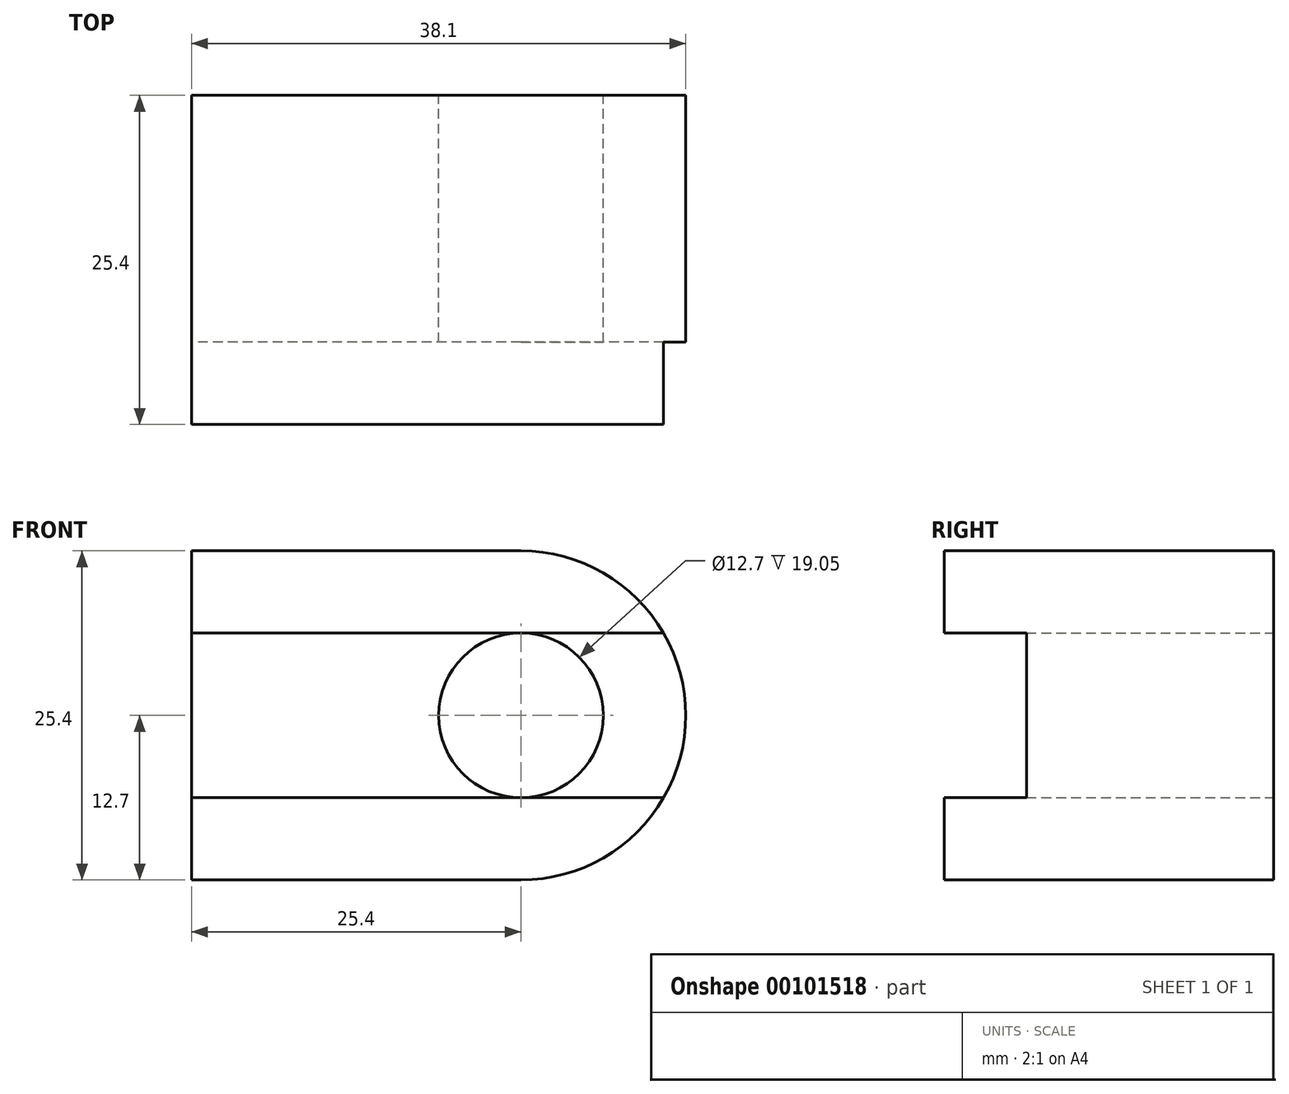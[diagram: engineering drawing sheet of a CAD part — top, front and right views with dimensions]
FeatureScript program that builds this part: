
annotation { "Feature Type Name" : "Feature", "Feature Type Description" : "" }
export const myFeature = defineFeature(function(context is Context, id is Id, definition is map)
    precondition{}
    {
        {
            var Q0;
            Q0=qCreatedBy(makeId("Top.planeOp"),FACE);
            var sketch = newSketch(context, id + "F0", { "sketchPlane" : qUnion([Q0])});
            skLineSegment(sketch, "E0.bottom", {"start": v(0, 0) * mm, "end": v(38.1, 0) * mm});
            skLineSegment(sketch, "E0.top", {"start": v(0, -25.4) * mm, "end": v(38.1, -25.4) * mm});
            skLineSegment(sketch, "E0.left", {"start": v(0, 0) * mm, "end": v(0, -25.4) * mm});
            skLineSegment(sketch, "E0.right", {"start": v(38.1, 0) * mm, "end": v(38.1, -25.4) * mm});
            skLineSegment(sketch, "E1.bottom", {"start": v(0, 0) * mm, "end": v(12.7, 0) * mm});
            skLineSegment(sketch, "E1.top", {"start": v(0, -12.7) * mm, "end": v(12.7, -12.7) * mm});
            skLineSegment(sketch, "E1.left", {"start": v(0, 0) * mm, "end": v(0, -12.7) * mm});
            skLineSegment(sketch, "E1.right", {"start": v(12.7, 0) * mm, "end": v(12.7, -12.7) * mm});
            skLineSegment(sketch, "E2.bottom", {"start": v(12.7, -12.7) * mm, "end": v(38.1, -12.7) * mm});
            skLineSegment(sketch, "E2.top", {"start": v(12.7, -25.4) * mm, "end": v(38.1, -25.4) * mm});
            skLineSegment(sketch, "E2.left", {"start": v(12.7, -12.7) * mm, "end": v(12.7, -25.4) * mm});
            skLineSegment(sketch, "E2.right", {"start": v(38.1, -12.7) * mm, "end": v(38.1, -25.4) * mm});
            skSolve(sketch);
        }
        {
            var Q0;
            Q0=makeQuery(id+"F0.imprint","IMPRINT",FACE,{"disambiguationData":[TD([[makeQuery(id+"F0.imprint","IMPRINT",EDGE,{"derivedFrom":sQuery(id+"F0.wireOp",EDGE,"E0.bottom")}),-1.0]])]});
            var Q1;
            Q1=makeQuery(id+"F0.imprint","IMPRINT",FACE,{"disambiguationData":[TD([[makeQuery(id+"F0.imprint","IMPRINT",EDGE,{"derivedFrom":sQuery(id+"F0.wireOp",EDGE,"E0.top")}),1.0]])]});
            var Q2;
            Q2=makeQuery(id+"F0.imprint","IMPRINT",FACE,{"disambiguationData":[TD([[makeQuery(id+"F0.imprint","IMPRINT",EDGE,{"derivedFrom":sQuery(id+"F0.wireOp",EDGE,"E1.bottom")}),-1.0]])]});
            extrude(context, id + "F1", {"entities" : qUnion([Q0, Q1, Q2]), "depth" : 25.4 * mm});
        }
        {
            var Q0;
            Q0=qCreatedBy(makeId("Right.planeOp"),FACE);
            var sketch = newSketch(context, id + "F2", { "sketchPlane" : qUnion([Q0])});
            skLineSegment(sketch, "E3.bottom", {"start": v(0, 0) * mm, "end": v(-19.05, 0) * mm});
            skLineSegment(sketch, "E3.top", {"start": v(0, 6.35) * mm, "end": v(-19.05, 6.35) * mm});
            skLineSegment(sketch, "E3.left", {"start": v(0, 0) * mm, "end": v(0, 6.35) * mm});
            skLineSegment(sketch, "E3.right", {"start": v(-19.05, 0) * mm, "end": v(-19.05, 6.35) * mm});
            skLineSegment(sketch, "E4.bottom", {"start": v(-19.05, 6.35) * mm, "end": v(-25.4, 6.35) * mm});
            skLineSegment(sketch, "E4.top", {"start": v(-19.05, 19.05) * mm, "end": v(-25.4, 19.05) * mm});
            skLineSegment(sketch, "E4.left", {"start": v(-19.05, 6.35) * mm, "end": v(-19.05, 19.05) * mm});
            skLineSegment(sketch, "E4.right", {"start": v(-25.4, 6.35) * mm, "end": v(-25.4, 19.05) * mm});
            skSolve(sketch);
        }
        {
            var Q0;
            Q0=makeQuery(id+"F2.imprint","IMPRINT",FACE,{"disambiguationData":[TD([[makeQuery(id+"F2.imprint","IMPRINT",EDGE,{"derivedFrom":sQuery(id+"F2.wireOp",EDGE,"E4.bottom")}),-1.0]])]});
            extrude(context, id + "F3", {"entities" : qUnion([Q0]), "operationType" : NewBodyOperationType.REMOVE, "endBound" : BoundingType.THROUGH_ALL, "depth" : 25.4 * mm});
        }
        {
            var Q0;
            Q0=qCreatedBy(makeId("Front.planeOp"),FACE);
            var sketch = newSketch(context, id + "F4", { "sketchPlane" : qUnion([Q0])});
            skCircle(sketch, "E5", {"center": v(25.4, 12.7) * mm, "radius": 6.35 * mm});
            skSolve(sketch);
        }
        {
            var Q0;
            Q0 = qSketchRegion(id + "F4", true);
            extrude(context, id + "F5", {"entities" : qUnion([Q0]), "operationType" : NewBodyOperationType.REMOVE, "endBound" : BoundingType.THROUGH_ALL, "depth" : 25.4 * mm});
        }
        {
            var Q0;
            Q0=qCreatedBy(makeId("Front.planeOp"),FACE);
            var sketch = newSketch(context, id + "F6", { "sketchPlane" : qUnion([Q0])});
            skLineSegment(sketch, "E6.bottom", {"start": v(0, 0) * mm, "end": v(25.4, 0) * mm});
            skLineSegment(sketch, "E6.top", {"start": v(0, 25.4) * mm, "end": v(25.4, 25.4) * mm});
            skLineSegment(sketch, "E6.left", {"start": v(0, 0) * mm, "end": v(0, 25.4) * mm});
            skLineSegment(sketch, "E6.right", {"start": v(25.4, 0) * mm, "end": v(25.4, 25.4) * mm});
            skArc(sketch, "E7", {"start": v(25.4, 0) * mm, "mid": v(38.1, 12.7) * mm, "end": v(25.4, 25.4) * mm});
            skLineSegment(sketch, "E8", {"start": v(25.4, 25.4) * mm, "end": v(38.1, 25.4) * mm});
            skLineSegment(sketch, "E9", {"start": v(38.1, 25.4) * mm, "end": v(38.1, 0) * mm});
            skLineSegment(sketch, "E10", {"start": v(38.1, 0) * mm, "end": v(25.4, 0) * mm});
            skSolve(sketch);
        }
        {
            var Q0;
            {var subQ0=sQuery(id+"F6.wireOp",EDGE,"E10");Q0=makeQuery(id+"F6.imprint","IMPRINT",FACE,{"disambiguationData":[TD([[makeQuery(id+"F6.imprint","IMPRINT",EDGE,{"derivedFrom":subQ0}),-1.0]])]});}
            var Q1;
            {var subQ0=sQuery(id+"F6.wireOp",EDGE,"E8");Q1=makeQuery(id+"F6.imprint","IMPRINT",FACE,{"disambiguationData":[TD([[makeQuery(id+"F6.imprint","IMPRINT",EDGE,{"derivedFrom":subQ0}),-1.0]])]});}
            extrude(context, id + "F7", {"entities" : qUnion([Q0, Q1]), "operationType" : NewBodyOperationType.REMOVE, "endBound" : BoundingType.THROUGH_ALL, "depth" : 25.4 * mm});
        }
    });
